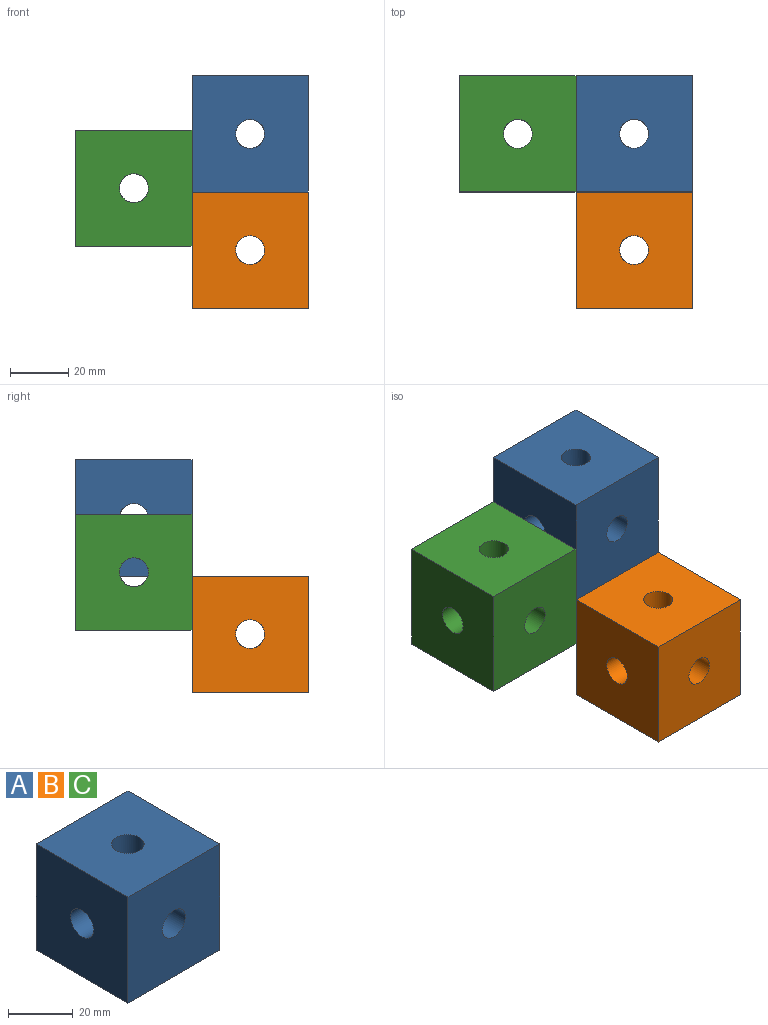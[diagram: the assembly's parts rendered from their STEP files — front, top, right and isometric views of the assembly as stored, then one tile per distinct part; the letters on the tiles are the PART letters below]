
ASSEMBLY  parts=3 mates=2
PART A: 12 faces, bbox 40x40x40 mm
  f0: cylinder r=5mm len=16.46mm, axis (0,0,1), area 486.9mm2, adj f2,f3,f5,f10,f11
  f1: cylinder r=5mm len=16.46mm, axis (0,0,1), area 486.9mm2, adj f2,f3,f7,f10,f11
  f2: cylinder r=5mm len=16.46mm, axis (0,1,0), area 486.9mm2, adj f0,f1,f9,f10,f11
  f3: cylinder r=5mm len=16.46mm, axis (0,1,0), area 486.9mm2, adj f0,f1,f8,f10,f11
  f4: plane 40x40mm, normal (1,0,0), area 1521.5mm2, adj f5,f7,f8,f9,f10
  f5: plane 40x40mm, normal (0,0,1), area 1521.5mm2, adj f0,f4,f6,f8,f9
  f6: plane 40x40mm, normal (-1,0,0), area 1521.5mm2, adj f5,f7,f8,f9,f11
  f7: plane 40x40mm, normal (0,0,-1), area 1521.5mm2, adj f1,f4,f6,f8,f9
  f8: plane 40x40mm, normal (0,-1,0), area 1521.5mm2, adj f3,f4,f5,f6,f7
  f9: plane 40x40mm, normal (0,1,0), area 1521.5mm2, adj f2,f4,f5,f6,f7
  f10: cylinder r=5mm len=16.46mm, axis (-1,0,0), area 486.9mm2, adj f0,f1,f2,f3,f4
  f11: cylinder r=5mm len=16.46mm, axis (-1,0,0), area 486.9mm2, adj f0,f1,f2,f3,f6
PART B: same geometry as A
PART C: same geometry as A
PLACE A at identity fixed
PLACE B t=(0,-40,-40)mm
PLACE C rot(axis=(0,1,0),180deg) t=(-80,0,21.3)mm
MATE fastened A.f8 <-> B.f9  axis (0,1,0) through (-40,-40,0)mm
MATE slider A.f5 <-> C.f7  axis (0,0,-1) through (-40,-40,40)mm
